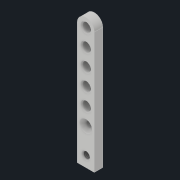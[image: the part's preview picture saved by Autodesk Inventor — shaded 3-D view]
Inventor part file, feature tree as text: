
AUTODESK INVENTOR PART (.ipt)
format: ipt  version: 2021.1 (Build 251245000, 245)  size: 137,216 bytes
history: native  units: in
note: dims shown in document units (in); Inventor stores cm internally (conversion verified against a paired STEP export)
features: sketch x4, hole x3, pattern_linear x1, fillet x1, chamfer x1
ambient origin geometry x8: Origin, YZ Plane, XZ Plane, XY Plane, X Axis, Y Axis, Z Axis, Center Point
bodies: Solid1 (feature_tree), Body (feature_tree)
feature tree (10):
  hole  "QBot Mount Hole"  [1 undecoded]
  hole  "Plate Mount Hole"  [1 undecoded]
  hole  "Axle Hole"  [1 undecoded]
  pattern_linear  "Rectangular Pattern1"  Spacing1=0.75in  [1 undecoded]
  fillet  "Fillet1"  Radius=0.25in
  chamfer  "Chamfer1"  Distance=0.5in
  sketch  "Sketch1"  dims[d0=0.5in d1=3.8125in]
  sketch  "Sketch2"  dims[d2=0.25in d3=0.0in d4=0.25in]
  sketch  "Sketch3"  dims[d5=0.3in]
  sketch  "Sketch4"  dims[d6=0.194in d7=0.472in d8=0.25in d9=0.25in d10=90.0deg d11=0.673in d12=0.8108in d13=0.25in d14=0.75in d15=0.169in d16=0.75in d17=0.37in d18=0.181in d19=90.0deg d20=1.0in d21=0.8108in d22=0.25in d23=0.5in d24=0.25in d25=0.75in d26=0.119in d27=0.181in d28=0.5635in d29=1.0in d30=0.8108in d31=1.9685in d33=0.5in d34=0.25in d35=0.252in d36=0.3in d37=0.0312in d38=0.125in d39=45.0deg]
note: 4 required parameter values undecoded (feature->parameter linkage not recoverable at this tier; creation-order binding heuristic only, values carry confidence <= 0.55)
